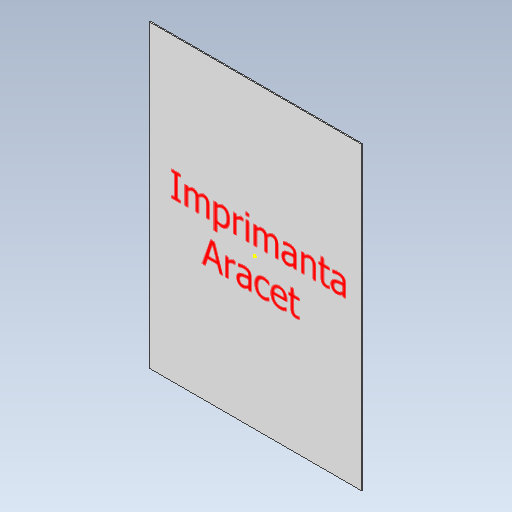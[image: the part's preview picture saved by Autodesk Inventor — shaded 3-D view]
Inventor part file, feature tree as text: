
AUTODESK INVENTOR PART (.ipt)
format: ipt  version: 2020 (Build 240168000, 168)  size: 97,792 bytes
history: native  units: mm
features: sketch x2, extrude x1
ambient origin geometry x8: Origin, YZ Plane, XZ Plane, XY Plane, X Axis, Y Axis, Z Axis, Center Point
bodies: Solid1 (feature_tree)
feature tree (3):
  extrude  "Extrusion1"  Depth=297.0mm
  sketch  "Sketch2"  dims[d2=1.0mm d3=0.0mm]
  sketch  "Sketch1"  dims[d0=210.0mm d1=297.0mm]
